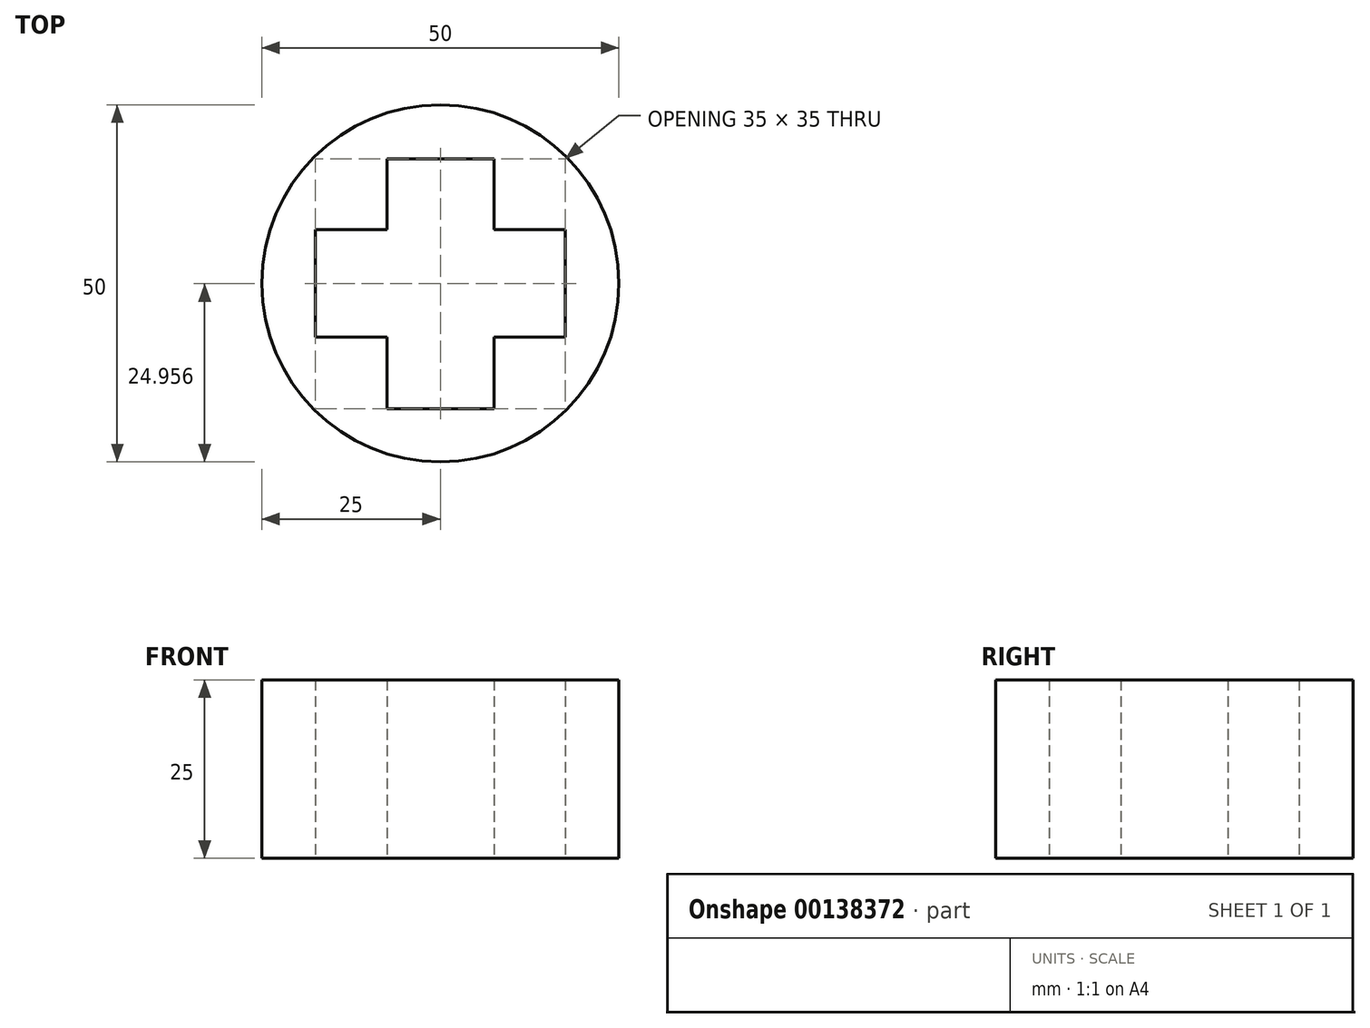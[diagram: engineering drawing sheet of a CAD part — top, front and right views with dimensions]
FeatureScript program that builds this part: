
annotation { "Feature Type Name" : "Feature", "Feature Type Description" : "" }
export const myFeature = defineFeature(function(context is Context, id is Id, definition is map)
    precondition{}
    {
        {
            var Q0;
            Q0=qCreatedBy(makeId("Top.planeOp"),FACE);
            var sketch = newSketch(context, id + "F0", { "sketchPlane" : qUnion([Q0])});
            skCircle(sketch, "E0", {"center": v(0, 0) * mm, "radius": 25 * mm});
            skCircle(sketch, "E1", {"center": v(0, 0) * mm, "radius": 4 * mm});
            skLineSegment(sketch, "E2.bottom", {"start": v(17.5, -7.5) * mm, "end": v(-17.5, -7.5) * mm});
            skLineSegment(sketch, "E2.top", {"start": v(17.5, 7.5) * mm, "end": v(-17.5, 7.5) * mm});
            skLineSegment(sketch, "E2.left", {"start": v(17.5, -7.5) * mm, "end": v(17.5, 7.5) * mm});
            skLineSegment(sketch, "E2.right", {"start": v(-17.5, -7.5) * mm, "end": v(-17.5, 7.5) * mm});
            skLineSegment(sketch, "E3.bottom", {"start": v(-20.33, -53.8) * mm, "end": v(-55.33, -53.8) * mm});
            skLineSegment(sketch, "E3.top", {"start": v(-20.33, -38.8) * mm, "end": v(-55.33, -38.8) * mm});
            skLineSegment(sketch, "E3.left", {"start": v(-20.33, -53.8) * mm, "end": v(-20.33, -38.8) * mm});
            skLineSegment(sketch, "E3.right", {"start": v(-55.33, -53.8) * mm, "end": v(-55.33, -38.8) * mm});
            skPoint(sketch, "E3.middle", {"position": v(-37.83, -46.3) * mm});
            skCircle(sketch, "E4", {"center": v(0, -0.04) * mm, "radius": 4 * mm});
            skLineSegment(sketch, "E5.bottom", {"start": v(-7.5, -17.54) * mm, "end": v(-7.5, 17.46) * mm});
            skLineSegment(sketch, "E5.top", {"start": v(7.5, -17.54) * mm, "end": v(7.5, 17.46) * mm});
            skLineSegment(sketch, "E5.left", {"start": v(-7.5, -17.54) * mm, "end": v(7.5, -17.54) * mm});
            skLineSegment(sketch, "E5.right", {"start": v(-7.5, 17.46) * mm, "end": v(7.5, 17.46) * mm});
            skSolve(sketch);
        }
        {
            var Q0;
            Q0=makeQuery(id+"F0.imprint","IMPRINT",FACE,{"disambiguationData":[TD([[makeQuery(id+"F0.imprint","IMPRINT",EDGE,{"derivedFrom":sQuery(id+"F0.wireOp",EDGE,"E0")}),1.0]])]});
            extrude(context, id + "F1", {"entities" : qUnion([Q0]), "depth" : 25 * mm});
        }
    });
